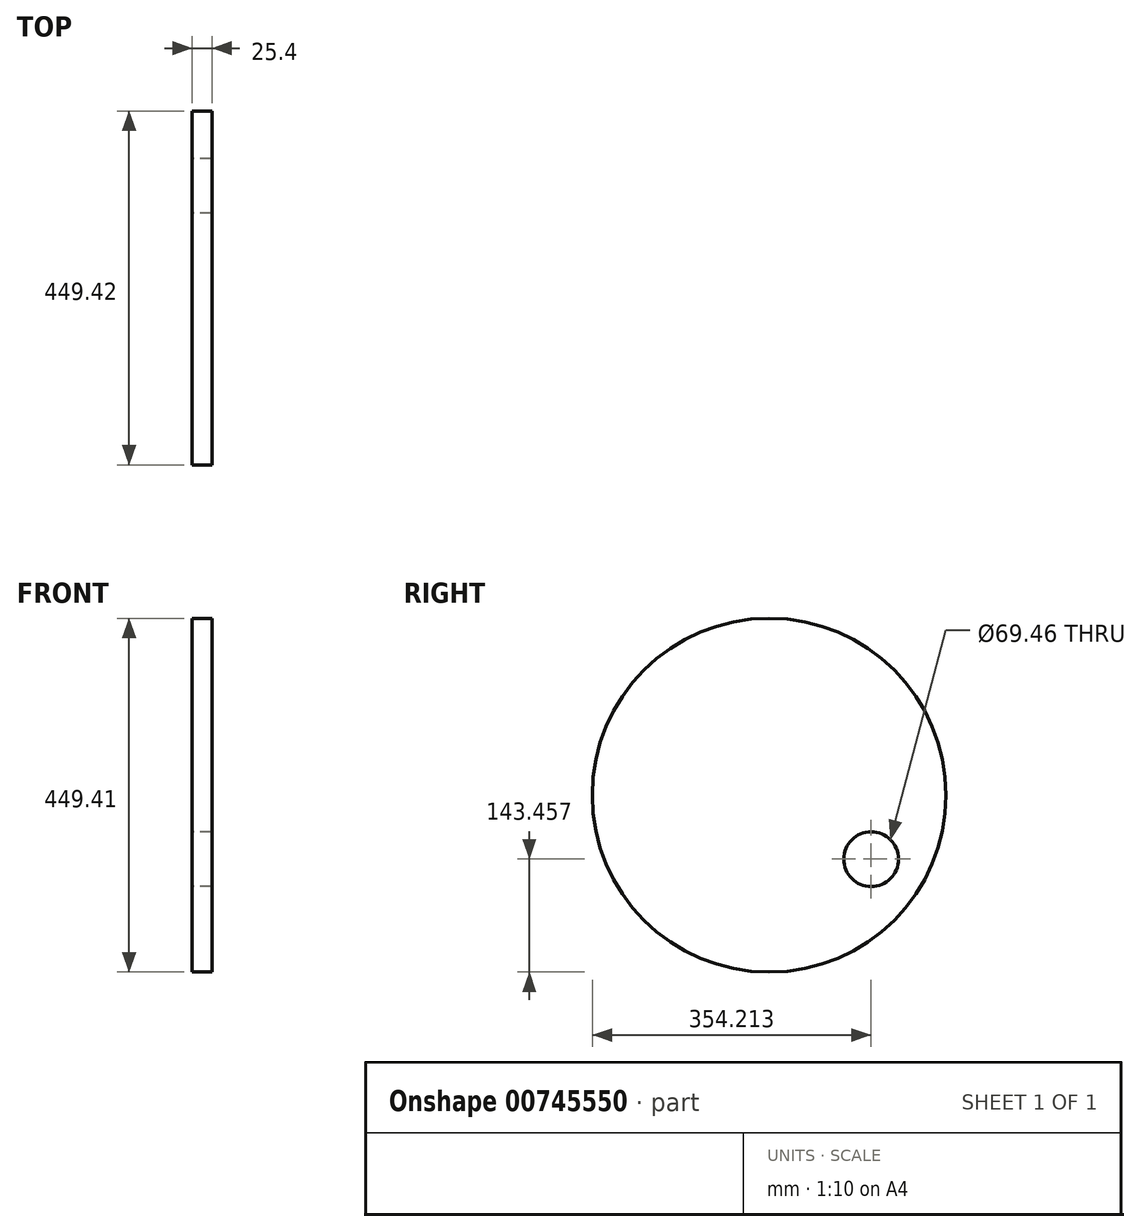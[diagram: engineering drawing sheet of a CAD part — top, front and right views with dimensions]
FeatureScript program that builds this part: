
annotation { "Feature Type Name" : "Feature", "Feature Type Description" : "" }
export const myFeature = defineFeature(function(context is Context, id is Id, definition is map)
    precondition{}
    {
        {
            var Q0;
            Q0=qCreatedBy(makeId("Right.planeOp"),FACE);
            var sketch = newSketch(context, id + "F0", { "sketchPlane" : qUnion([Q0])});
            skCircle(sketch, "E0", {"center": v(-10.95, -14.43) * mm, "radius": 34.73 * mm});
            skCircle(sketch, "E1", {"center": v(-140.45, 66.81) * mm, "radius": 224.7 * mm});
            skSolve(sketch);
        }
        {
            var Q0;
            Q0 = qSketchRegion(id + "F0", true);
            extrude(context, id + "F1", {"entities" : qUnion([Q0]), "depth" : 25.4 * mm, "offsetDistance" : 25.4 * mm});
        }
    });
